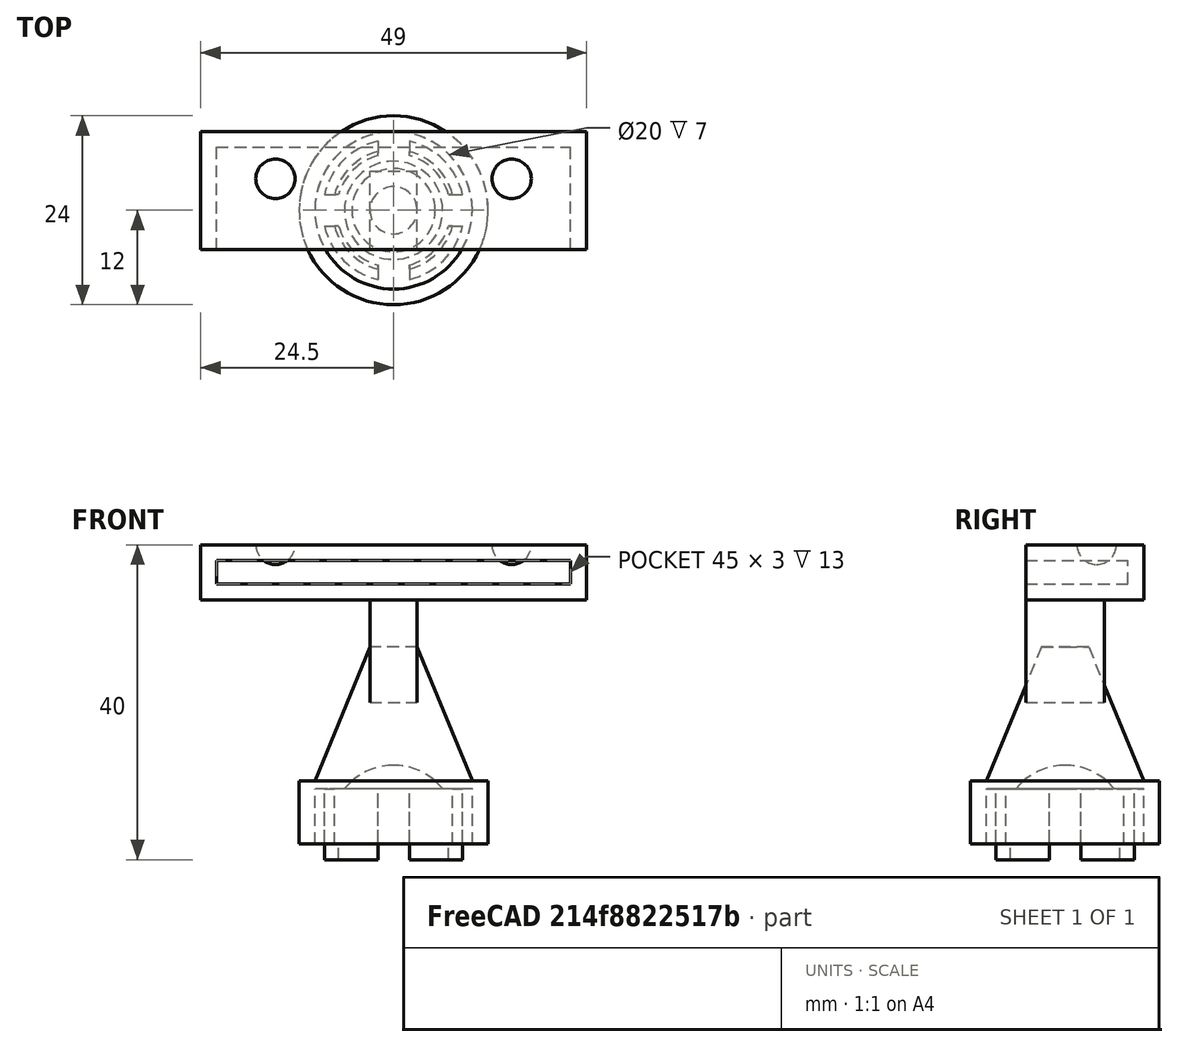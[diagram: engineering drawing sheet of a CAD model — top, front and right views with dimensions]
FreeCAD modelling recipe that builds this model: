
FCSTD DOCUMENT  (FreeCAD 0.14R2935 (Git))
Label: sylvanian-trailer-mount
License: CC-BY 3.0
LicenseURL: http://creativecommons.org/licenses/by/3.0/
objects: Part::Cut×9, Part::Cylinder×5, Part::Box×5, Part::Sphere×3, Part::Cone×1
note: 23 computed .brp shape members not serialized (recipe doc carries the construction recipe); baked Part::Feature solids carry a one-line shape summary decoded from their .brp

FEATURE [Part::Cylinder] Cylinder  label="fatning"
  Angle = 360
  Height = 8
  Radius = 12
FEATURE [Part::Cone] Cone  label="overgang, aksel, fatning"
  Angle = 360
  Height = 17
  Placement = pos=(0,0,8) rot=(0,0,1;0rad)
  Radius1 = 10
  Radius2 = 3
FEATURE [Part::Box] Box  label="aksel"
  Height = 13
  Length = 6
  Placement = pos=(-3,-5,18) rot=(0,0,1;0rad)
  Width = 10
FEATURE [Part::Box] Box001  label="ydre montering"
  Height = 7
  Length = 49
  Placement = pos=(-24.5,-5,35) rot=(0,0,1;0rad)
  Width = 15
FEATURE [Part::Box] Box002  label="ydre montering cutter"
  Height = 3
  Length = 45
  Placement = pos=(-22.5,-5,37) rot=(0,0,1;0rad)
  Width = 13
FEATURE [Part::Cut] Cut  label="Montering bil"
  Base = -> Box001
  Placement = pos=(0,0,-4) rot=(0,0,1;0rad)
  Tool = -> Box002
FEATURE [Part::Cylinder] Cylinder001  label="fatning cutter"
  Angle = 360
  Height = 8
  Placement = pos=(0,0,-1) rot=(0,0,1;0rad)
  Radius = 10
FEATURE [Part::Cut] Cut001  label="Cuttet fatning"
  Base = -> Cylinder
  Tool = -> Cylinder001
FEATURE [Part::Cut] Cut002  label="Cuttet overgang"
  Base = -> Cone
  Tool = -> Cylinder001
FEATURE [Part::Cylinder] Cylinder002  label="Holder dims, solid"
  Angle = 360
  Height = 9
  Placement = pos=(0,0,-2) rot=(0,0,1;0rad)
  Radius = 9
FEATURE [Part::Cylinder] Cylinder003  label="Holder dims, cutter indre"
  Angle = 360
  Height = 7
  Radius = 7.75
FEATURE [Part::Cut] Cut003
  Base = -> Cylinder002
  Tool = -> Cylinder003
FEATURE [Part::Cylinder] Cylinder004  label="Holder dims, cutter ydre/rund"
  Angle = 360
  Height = 7
  Placement = pos=(0,0,-5) rot=(0,0,1;0rad)
  Radius = 7.25
FEATURE [Part::Cut] Cut004  label="Fatning uden kryds cut"
  Base = -> Cut003
  Tool = -> Cylinder004
FEATURE [Part::Box] Box003  label="Kryds cut 1"
  Height = 9
  Length = 18
  Placement = pos=(-9,-2,-2) rot=(0,0,1;0rad)
  Width = 4
FEATURE [Part::Box] Box004  label="Kryds cut 2"
  Height = 9
  Length = 18
  Placement = pos=(-2,9,-2) rot=(0,0,-1;1.5708rad)
  Width = 4
FEATURE [Part::Cut] Cut005
  Base = -> Cut004
  Tool = -> Box003
FEATURE [Part::Cut] Cut006  label="Cuttet indre fatning"
  Base = -> Cut005
  Tool = -> Box004
FEATURE [Part::Sphere] Sphere  label="Bump 1"
  Angle1 = -90
  Angle2 = 0
  Angle3 = 360
  Placement = pos=(15,4,38) rot=(0,0,1;0rad)
  Radius = 2.5
FEATURE [Part::Sphere] Sphere001  label="Bump 2"
  Angle1 = -90
  Angle2 = 0
  Angle3 = 360
  Placement = pos=(-15,4,38) rot=(0,0,1;0rad)
  Radius = 2.5
FEATURE [Part::Sphere] Sphere002  label="Ball-thing cutter"
  Angle1 = -90
  Angle2 = 90
  Angle3 = 360
  Placement = pos=(0,0,2) rot=(0,0,1;0rad)
  Radius = 8
FEATURE [Part::Cut] Cut007  label="Fatning cuttet med kugle"
  Base = -> Cut001
  Tool = -> Sphere002
FEATURE [Part::Cut] Cut008  label="Transition and bottom of ball bearing, cutted"
  Base = -> Cut002
  Tool = -> Sphere002
